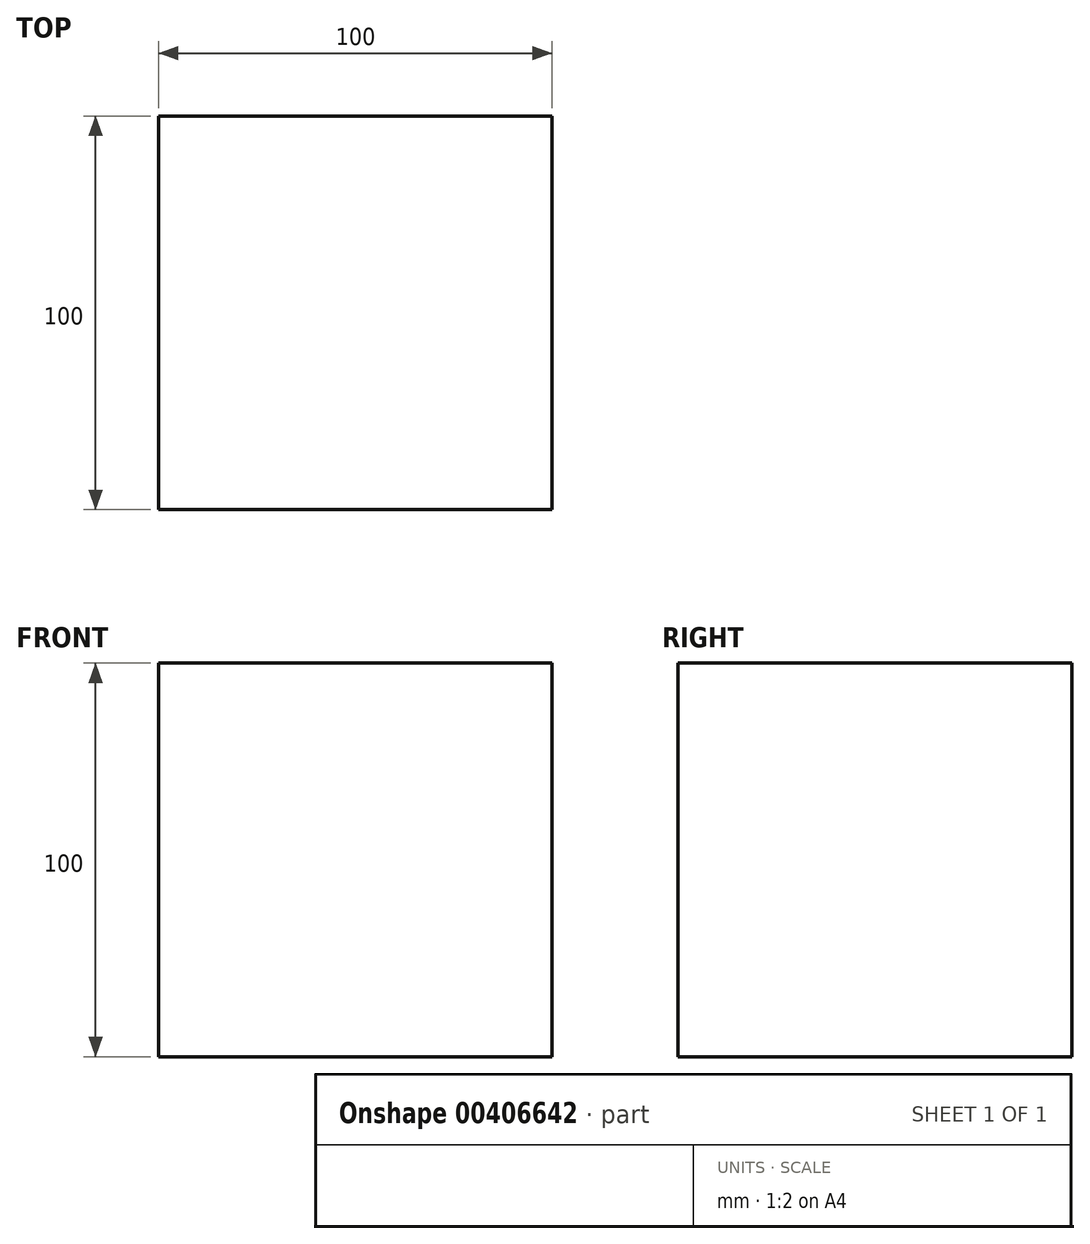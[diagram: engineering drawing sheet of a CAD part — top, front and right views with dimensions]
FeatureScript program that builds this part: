
annotation { "Feature Type Name" : "Feature", "Feature Type Description" : "" }
export const myFeature = defineFeature(function(context is Context, id is Id, definition is map)
    precondition{}
    {
        {
            var Q0;
            Q0=qCreatedBy(makeId("Top.planeOp"),FACE);
            var sketch = newSketch(context, id + "F0", { "sketchPlane" : qUnion([Q0])});
            skLineSegment(sketch, "E0.bottom", {"start": v(250, 250) * mm, "end": v(150, 250) * mm});
            skLineSegment(sketch, "E0.top", {"start": v(250, 150) * mm, "end": v(150, 150) * mm});
            skLineSegment(sketch, "E0.left", {"start": v(250, 250) * mm, "end": v(250, 150) * mm});
            skLineSegment(sketch, "E0.right", {"start": v(150, 250) * mm, "end": v(150, 150) * mm});
            skPoint(sketch, "E0.middle", {"position": v(200, 200) * mm});
            skSolve(sketch);
        }
        {
            var Q0;
            Q0=makeQuery(id+"F0.imprint","IMPRINT",FACE,{"disambiguationData":[TD([[makeQuery(id+"F0.imprint","IMPRINT",EDGE,{"derivedFrom":sQuery(id+"F0.wireOp",EDGE,"E0.bottom")}),1.0]])]});
            extrude(context, id + "F1", {"entities" : qUnion([Q0]), "depth" : 100 * mm});
        }
    });
